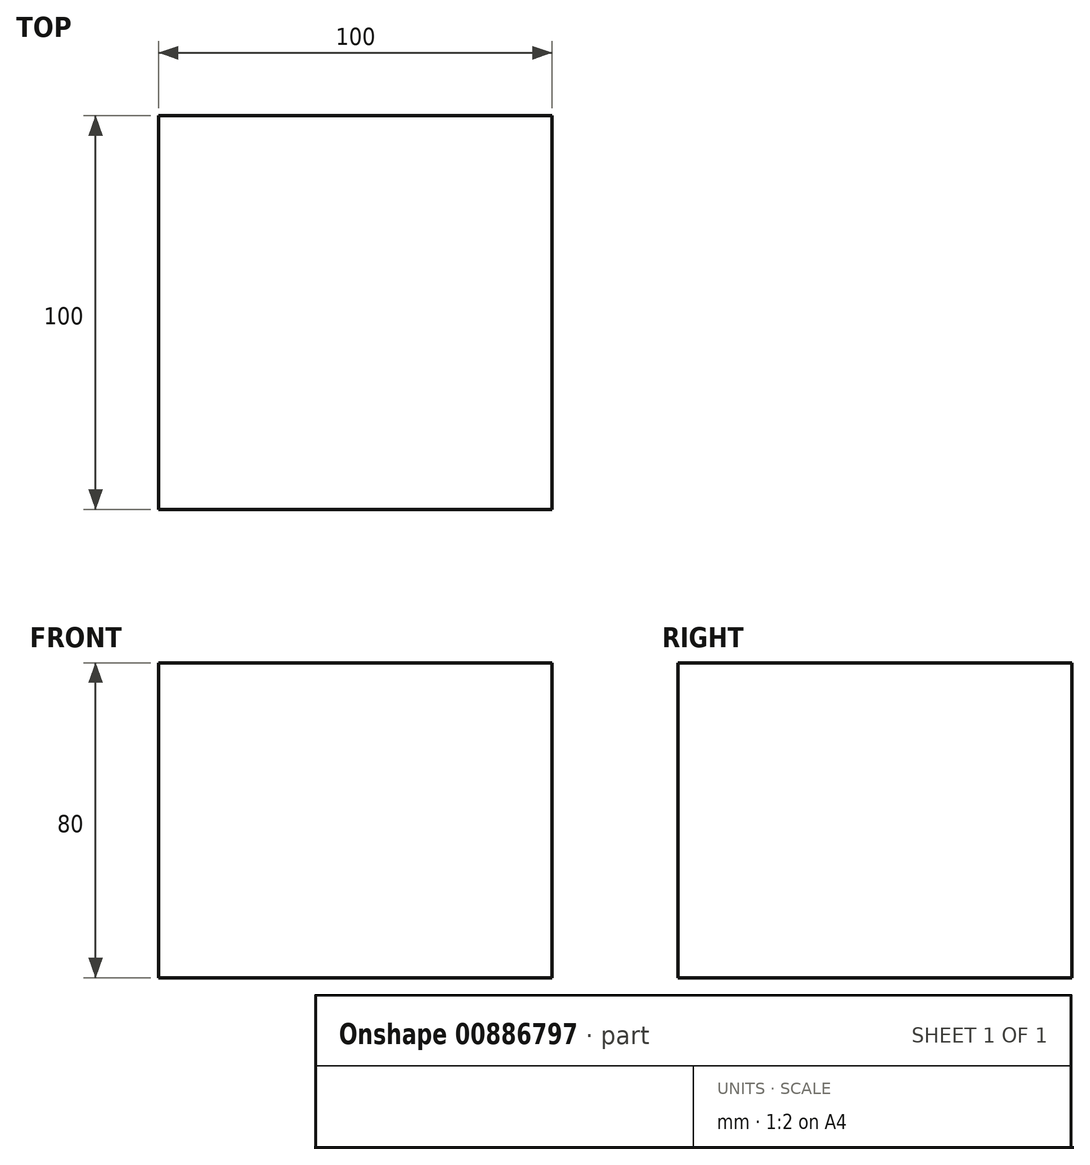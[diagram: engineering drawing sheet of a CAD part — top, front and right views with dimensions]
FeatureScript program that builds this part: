
annotation { "Feature Type Name" : "Feature", "Feature Type Description" : "" }
export const myFeature = defineFeature(function(context is Context, id is Id, definition is map)
    precondition{}
    {
        {
            var Q0;
            Q0=qCreatedBy(makeId("Front.planeOp"),FACE);
            var sketch = newSketch(context, id + "F0", { "sketchPlane" : qUnion([Q0])});
            skLineSegment(sketch, "E0.bottom", {"start": v(0, 80) * mm, "end": v(100, 80) * mm});
            skLineSegment(sketch, "E0.top", {"start": v(0, 0) * mm, "end": v(100, 0) * mm});
            skLineSegment(sketch, "E0.left", {"start": v(0, 80) * mm, "end": v(0, 0) * mm});
            skLineSegment(sketch, "E0.right", {"start": v(100, 80) * mm, "end": v(100, 0) * mm});
            skSolve(sketch);
        }
        {
            var Q0;
            Q0=makeQuery(id+"F0.imprint","IMPRINT",FACE,{"disambiguationData":[TD([[makeQuery(id+"F0.imprint","IMPRINT",EDGE,{"derivedFrom":sQuery(id+"F0.wireOp",EDGE,"E0.bottom")}),-1.0]])]});
            extrude(context, id + "F1", {"entities" : qUnion([Q0]), "depth" : 100 * mm, "offsetDistance" : 25.4 * mm});
        }
    });
